# Revit family: Haworth_Compose_Worksurface_Corner90Extended
name_source: partatom
category: Furniture Systems
revit_build: Autodesk Revit 2018 (Build: 20170223_1515(x64)
units: mm (PartAtom-declared; Revit-internal decimal feet)

## family parameters
Always vertical = Yes
Cut with Voids When Loaded = No
OmniClass Number = 23.40.70.14.64.21
OmniClass Title = Systems Furniture
Part Type = Normal
Room Calculation Point = No
Round Connector Dimension = Use Diameter
Shared = No
Work Plane-Based = No

## types (12) — shared parameters
Actual Height = 29"
Assembly Code = E2020200
Cantilever Bracket = No
Cantilever Bracket Location = 2"
Description = Haworth - Worksurface Compose Corner - 90 Extended
Double Support Leg = Yes
End Support Location = 1 3/4"
Height = 29"
Manufacturer = Haworth
Max. Depth = 30"
Max. Height = 48"
Max. Length = 72"
Max. Width = 60"
Min. Depth = 18"
Min. Height = 26"
Min. Length = 36"
Min. Width = 36"
Min/Max Length = 36-72 in. @ 6 in. increments
Min/Max Width = 36, 42, 48 in.
Model = WUCP
Revision Number = 3
Shared Cantilever Bracket = No
Size = Verify Final Dim. w/ Haworth
Standard Depths = 18, 24, 30 in.
Support Finish = Haworth _ Paint _ Undecided _ Panel
Support Height = 27 13/16"
Support Panel = No
Support Post_45 Degree = No
Support Post_90 Degree = No
Sustainability Info = http://media.haworth.com
Top Thickness = 1 3/16"
URL = www.haworth.com
URL - Product = http://www.haworth.com
Warranty = http://www.haworth.com
Worksurface Edge Finish = Haworth _ Laminate _ Undecided _ Panel
Worksurface Finish = Haworth _ Laminate _ Undecided _ Panel

## per-type parameters (varying)
| type | Actual Depth | Actual Length | Actual Width | Custom Size | Depth | Depth Narrow | Length | Radius | Width |
| 36L 36w 24d | 24" | 36" | 36" | Yes | 24" | 24" | 36" | 10 1/4" | 36" |
| 36L 36w 30d | 30" | 36" | 36" | Yes | 30" | 30" | 36" | 4 1/4" | 36" |
| 42L 42w 24d | 24" | 42" | 42" | No | 24" | 24" | 42" | 10 1/4" | 42" |
| 42L 42w 30d | 30" | 42" | 42" | No | 30" | 30" | 42" | 10 1/4" | 42" |
| 48L 48w 24d | 24" | 48" | 48" | No | 24" | 24" | 48" | 10 1/4" | 48" |
| 48L 48w 30d | 30" | 48" | 48" | No | 30" | 30" | 48" | 10 1/4" | 48" |
| 54L 48w 24d | 24" | 54" | 48" | No | 24" | 24" | 54" | 10 1/4" | 48" |
| 54L 54w 24d | 24" | 54" | 54" | No | 24" | 24" | 54" | 10 1/4" | 54" |
| 54L 54w 30d | 30" | 54" | 54" | No | 30" | 30" | 54" | 10 1/4" | 54" |
| 60L 48w 24d | 24" | 60" | 48" | No | 24" | 24" | 60" | 10 1/4" | 48" |
| 66L 48w 24d | 24" | 66" | 48" | No | 24" | 24" | 66" | 10 1/4" | 48" |
| 72L 48w 24d | 24" | 72" | 48" | No | 24" | 24" | 72" | 10 1/4" | 48" |

## geometry (parser evidence)
native form markers: Sweep x15
no freeform markers — native parametric forms only
